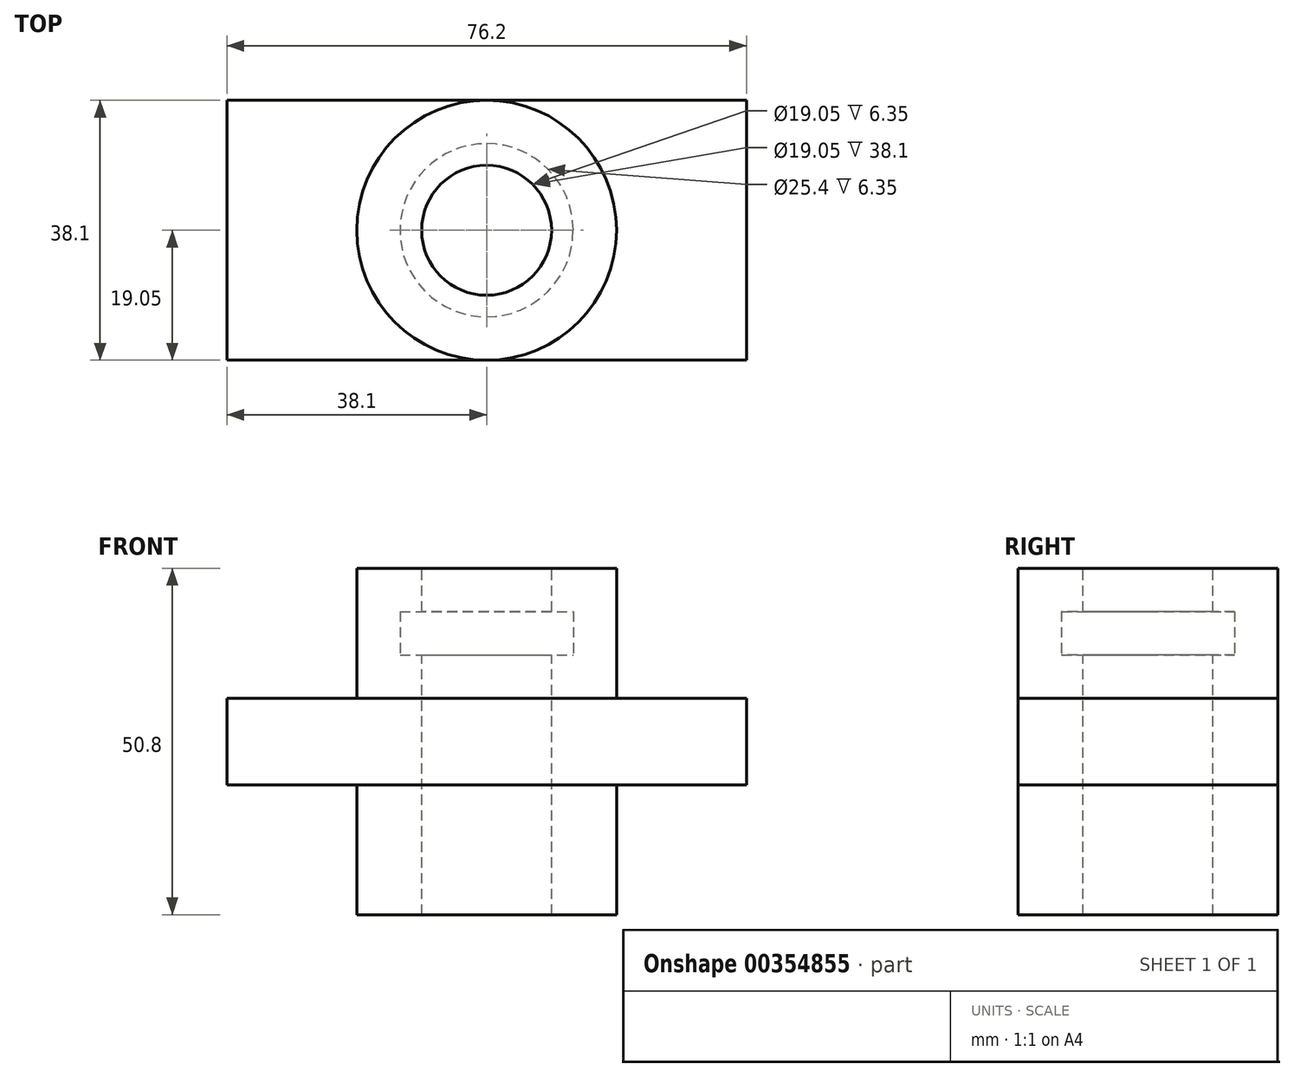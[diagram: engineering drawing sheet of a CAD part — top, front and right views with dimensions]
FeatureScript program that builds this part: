
annotation { "Feature Type Name" : "Feature", "Feature Type Description" : "" }
export const myFeature = defineFeature(function(context is Context, id is Id, definition is map)
    precondition{}
    {
        {
            var Q0;
            Q0=qCreatedBy(makeId("Top.planeOp"),FACE);
            var sketch = newSketch(context, id + "F0", { "sketchPlane" : qUnion([Q0])});
            skLineSegment(sketch, "E0", {"start": v(0, 19.05) * mm, "end": v(38.1, 19.05) * mm});
            skLineSegment(sketch, "E1", {"start": v(38.1, 19.05) * mm, "end": v(38.1, -19.05) * mm});
            skLineSegment(sketch, "E2", {"start": v(38.1, -19.05) * mm, "end": v(-38.1, -19.05) * mm});
            skLineSegment(sketch, "E3", {"start": v(-38.1, -19.05) * mm, "end": v(-38.1, 19.05) * mm});
            skLineSegment(sketch, "E4", {"start": v(-38.1, 19.05) * mm, "end": v(0, 19.05) * mm});
            skSolve(sketch);
        }
        {
            var Q0;
            Q0 = qSketchRegion(id + "F0", true);
            extrude(context, id + "F1", {"entities" : qUnion([Q0]), "oppositeDirection" : true, "depth" : 12.7 * mm});
        }
        {
            var Q0;
            Q0=qCreatedBy(makeId("Front.planeOp"),FACE);
            var sketch = newSketch(context, id + "F2", { "sketchPlane" : qUnion([Q0])});
            skLineSegment(sketch, "E5", {"start": v(0, 0) * mm, "end": v(0, 6.35) * mm});
            skLineSegment(sketch, "E6", {"start": v(0, 6.35) * mm, "end": v(-12.7, 6.35) * mm});
            skLineSegment(sketch, "E7", {"start": v(-12.7, 6.35) * mm, "end": v(-12.7, 12.7) * mm});
            skLineSegment(sketch, "E8", {"start": v(-12.7, 12.7) * mm, "end": v(0, 12.7) * mm});
            skLineSegment(sketch, "E9", {"start": v(0, 12.7) * mm, "end": v(0, 19.05) * mm});
            skLineSegment(sketch, "E10", {"start": v(0, 19.05) * mm, "end": v(-19.05, 19.05) * mm});
            skLineSegment(sketch, "E11", {"start": v(-19.05, 19.05) * mm, "end": v(-19.05, 0) * mm});
            skLineSegment(sketch, "E12", {"start": v(-19.05, 0) * mm, "end": v(0, 0) * mm});
            skLineSegment(sketch, "E13", {"start": v(0, 0) * mm, "end": v(0, 38.2) * mm, "construction": true});
            skSolve(sketch);
        }
        {
            var Q0;
            Q0 = qSketchRegion(id + "F2", true);
            var Q1;
            Q1=sQuery(id+"F2.wireOp",EDGE,"E13");
            revolve(context, id + "F3", {"operationType" : NewBodyOperationType.ADD, "entities" : qUnion([Q0]), "axis" : qUnion([Q1]), "revolveType" : RevolveType.FULL});
        }
        {
            var Q0;
            Q0=makeQuery(id+"F3.opRevolve","SWEPT_FACE",FACE,{"disambiguationData":[OSD([sQuery(id+"F2.wireOp",EDGE,"E10")])]});
            var sketch = newSketch(context, id + "F4", { "sketchPlane" : qUnion([Q0])});
            skCircle(sketch, "E14", {"center": v(0, 0) * mm, "radius": 9.53 * mm});
            skSolve(sketch);
        }
        {
            var Q0;
            Q0 = qSketchRegion(id + "F4", true);
            extrude(context, id + "F5", {"entities" : qUnion([Q0]), "operationType" : NewBodyOperationType.REMOVE, "endBound" : BoundingType.THROUGH_ALL, "oppositeDirection" : true, "depth" : 25.4 * mm});
        }
        {
            var Q0;
            Q0=makeQuery(id+"F1.opExtrude","CAP_FACE",FACE,{"disambiguationData":[OSD([sQuery(id+"F0.wireOp",EDGE,"E0"),sQuery(id+"F0.wireOp",EDGE,"E1"),sQuery(id+"F0.wireOp",EDGE,"E2"),sQuery(id+"F0.wireOp",EDGE,"E3"),sQuery(id+"F0.wireOp",EDGE,"E4")])],"isStart":false});
            var sketch = newSketch(context, id + "F6", { "sketchPlane" : qUnion([Q0])});
            skCircle(sketch, "E15", {"center": v(0, 0) * mm, "radius": 19.05 * mm});
            skSolve(sketch);
        }
        {
            var Q0;
            Q0 = qSketchRegion(id + "F6", true);
            extrude(context, id + "F7", {"entities" : qUnion([Q0]), "operationType" : NewBodyOperationType.ADD, "depth" : 19.05 * mm});
        }
        {
            var Q0;
            Q0=makeQuery(id+"F7.opExtrude","CAP_FACE",FACE,{"disambiguationData":[OSD([sQuery(id+"F6.wireOp",EDGE,"E15")])],"isStart":false});
            var sketch = newSketch(context, id + "F8", { "sketchPlane" : qUnion([Q0])});
            skCircle(sketch, "E16", {"center": v(0, 0) * mm, "radius": 9.53 * mm});
            skSolve(sketch);
        }
        {
            var Q0;
            Q0 = qSketchRegion(id + "F8", true);
            extrude(context, id + "F9", {"entities" : qUnion([Q0]), "operationType" : NewBodyOperationType.REMOVE, "endBound" : BoundingType.THROUGH_ALL, "oppositeDirection" : true, "depth" : 25.4 * mm});
        }
    });
